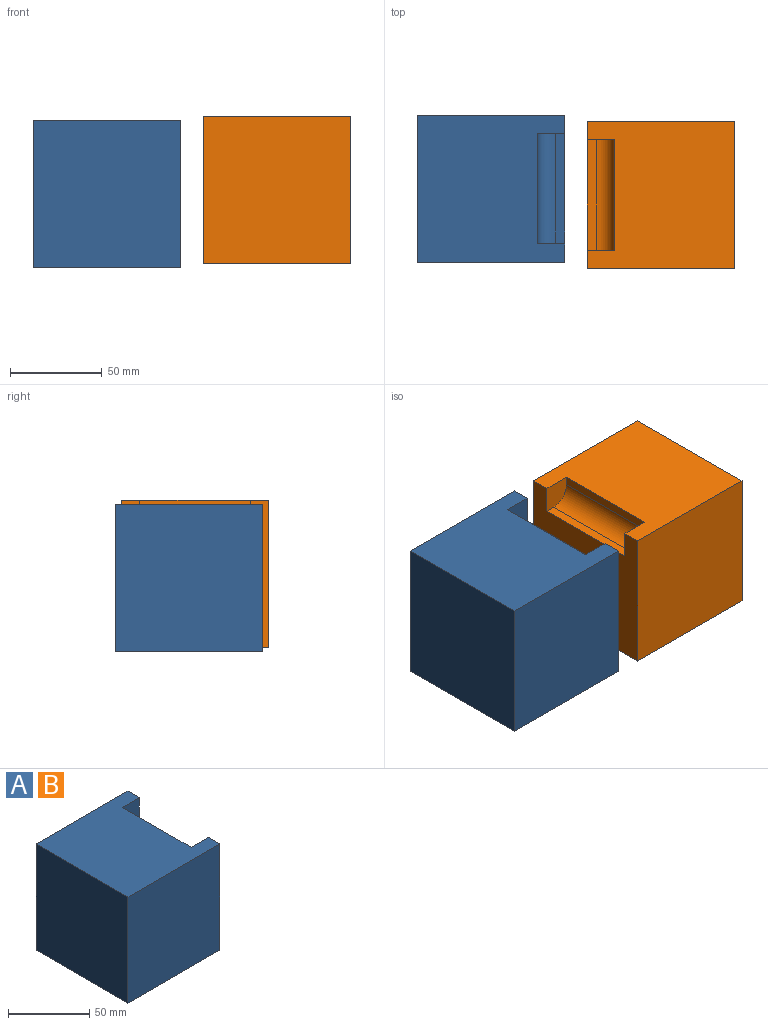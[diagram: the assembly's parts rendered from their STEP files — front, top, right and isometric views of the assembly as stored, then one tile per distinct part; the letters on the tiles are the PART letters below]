
ASSEMBLY  parts=2 mates=1
PART A: 11 faces, bbox 80x80x80 mm
  f0: plane 80x80mm, normal (0,1,0), area 6400mm2, adj f1,f3,f4,f5
  f1: plane 80x80mm, normal (-1,0,0), area 6400mm2, adj f0,f2,f4,f5
  f2: plane 80x80mm, normal (0,-1,0), area 6400mm2, adj f1,f3,f4,f5
  f3: plane 80x80mm, normal (1,0,0), area 5500mm2, adj f0,f2,f4,f5,f8,f9,f10
  f4: plane 80x80mm, normal (0,0,1), area 5500mm2, adj f0,f1,f2,f3,f6,f9,f10
  f5: plane 80x80mm, normal (0,0,-1), area 6400mm2, adj f0,f1,f2,f3
  f6: plane 60x5mm, normal (1,0,0), area 300mm2, adj f4,f7,f9,f10
  f7: cylinder r=10mm len=60mm, axis (0,1,0), area 942.5mm2, adj f6,f8,f9,f10
  f8: plane 60x5mm, normal (0,0,1), area 300mm2, adj f3,f7,f9,f10
  f9: plane 15x15mm, normal (0,1,0), area 203.5mm2, adj f3,f4,f6,f7,f8
  f10: plane 15x15mm, normal (0,-1,0), area 203.5mm2, adj f3,f4,f6,f7,f8
PART B: same geometry as A
PLACE A t=(91.11,19.7,-16.4)mm
PLACE B rot(axis=(0,0,1),180deg) t=(183.09,16.37,-14.02)mm
MATE parallel B.f3 <-> A.f3  axis (-1,0,0) through (143.09,16.37,20.66)mm
